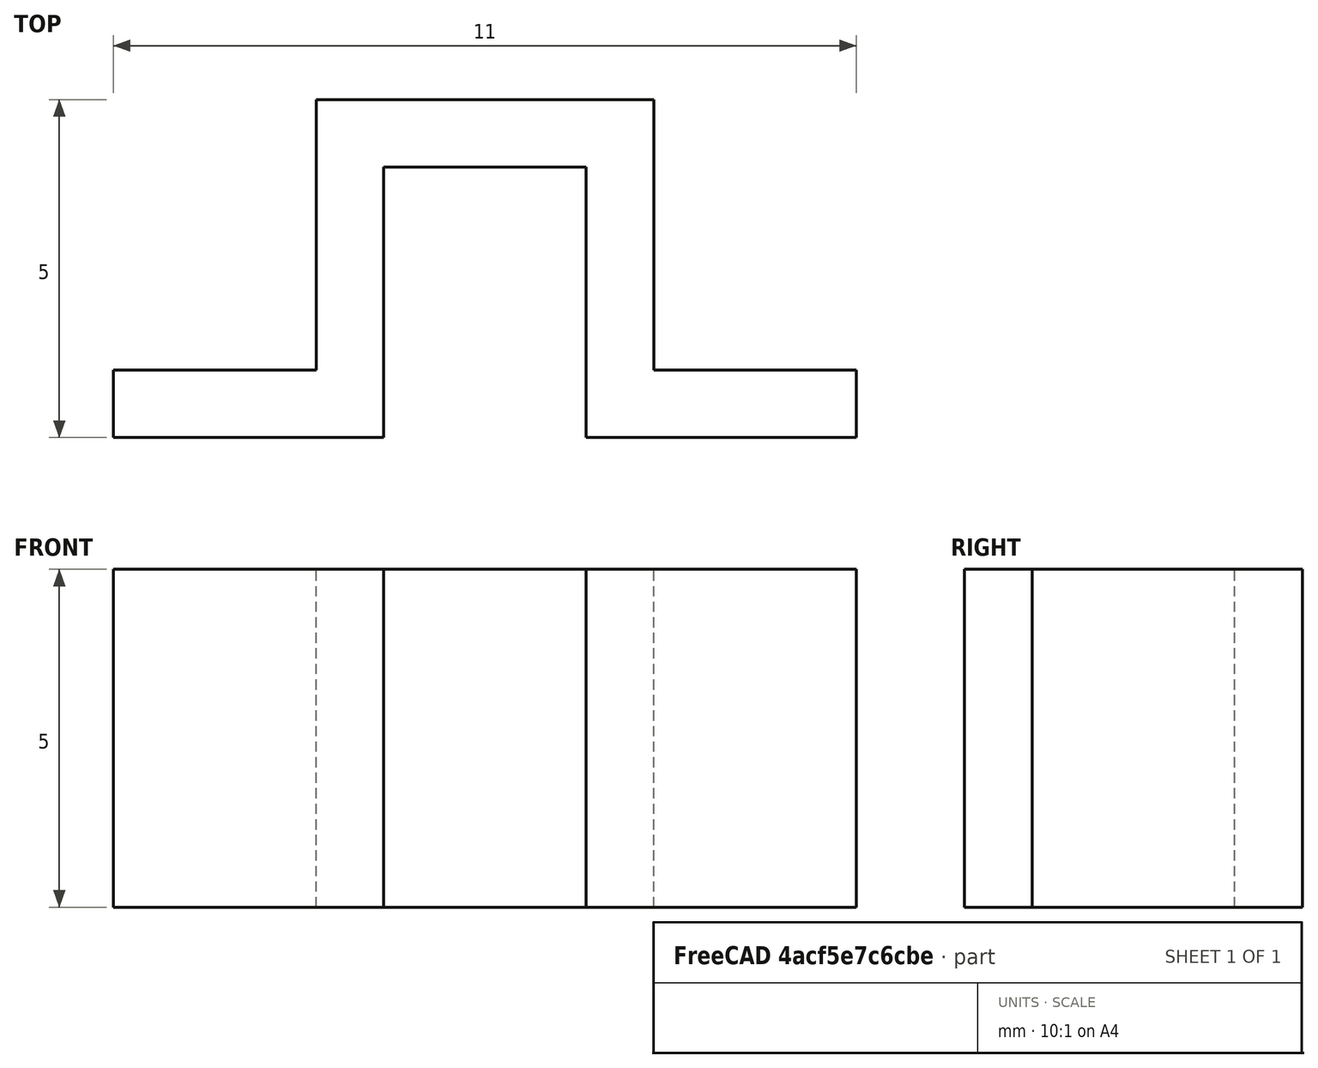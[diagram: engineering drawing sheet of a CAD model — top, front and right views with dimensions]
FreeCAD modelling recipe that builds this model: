
FCSTD DOCUMENT  (FreeCAD 0.19R)
Label: cable-clip
License: All rights reserved
LicenseURL: http://en.wikipedia.org/wiki/All_rights_reserved
objects: Sketcher::SketchObject×1, PartDesign::Pad×1, PartDesign::Body×1
note: 4 computed .brp shape members not serialized (recipe doc carries the construction recipe); baked Part::Feature solids carry a one-line shape summary decoded from their .brp

FEATURE [Sketcher::SketchObject] Sketch
  FullyConstrained = true
  MapMode = 5
  Support = -> [XY_Plane]
  sketch-geometry (13):
    g0: LineSegment StartX=0 StartY=0 StartZ=0 EndX=0 EndY=1 EndZ=0
    g1: LineSegment StartX=0 StartY=1 StartZ=0 EndX=3 EndY=1 EndZ=0
    g2: LineSegment StartX=3 StartY=1 StartZ=0 EndX=3 EndY=5 EndZ=0
    g3: LineSegment StartX=3 StartY=5 StartZ=0 EndX=8 EndY=5 EndZ=0
    g4: LineSegment StartX=8 StartY=5 StartZ=0 EndX=8 EndY=1 EndZ=0
    g5: LineSegment StartX=8 StartY=1 StartZ=0 EndX=11 EndY=1 EndZ=0
    g6: LineSegment StartX=11 StartY=1 StartZ=0 EndX=11 EndY=0 EndZ=0
    g7: LineSegment StartX=11 StartY=0 StartZ=0 EndX=7 EndY=0 EndZ=0
    g8: LineSegment StartX=7 StartY=0 StartZ=0 EndX=7 EndY=4 EndZ=0
    g9: LineSegment StartX=7 StartY=4 StartZ=0 EndX=4 EndY=4 EndZ=0
    g10: LineSegment StartX=4 StartY=4 StartZ=0 EndX=4 EndY=0 EndZ=0
    g11: LineSegment StartX=4 StartY=0 StartZ=0 EndX=0 EndY=0 EndZ=0
    g12: LineSegment StartX=5.5 StartY=5 StartZ=0 EndX=5.5 EndY=0 EndZ=0
  constraints (37):
    c: Coincident(g0,g-1)
    c: PointOnObject(g0,g-2)
    c: Coincident(g1,g0)
    c: Horizontal(g1)
    c: Coincident(g2,g1)
    c: Coincident(g3,g2)
    c: Horizontal(g3)
    c: Coincident(g4,g3)
    c: Vertical(g4)
    c: Coincident(g5,g4)
    c: Horizontal(g5)
    c: Coincident(g6,g5)
    c: PointOnObject(g6,g-1)
    c: Vertical(g6)
    c: Coincident(g7,g6)
    c: PointOnObject(g7,g-1)
    c: Coincident(g8,g7)
    c: Vertical(g8)
    c: Coincident(g9,g8)
    c: Coincident(g10,g9)
    c: PointOnObject(g10,g-1)
    c: Vertical(g10)
    c: Coincident(g11,g10)
    c: Coincident(g11,g0)
    c: Vertical(g2)
    c: DistanceX(g3,g3) = 5
    c: DistanceY(g9,g2) = 1
    c: DistanceX(g2,g9) = 1
    c: PointOnObject(g12,g3)
    c: PointOnObject(g12,g-1)
    c: Symmetric(g2,g3,g12)
    c: Symmetric(g9,g8,g12)
    c: DistanceY(g2,g2) = 4
    c: Equal(g0,g6)
    c: DistanceY(g0,g0) = 1
    c: Equal(g1,g5)
    c: DistanceX(g1,g1) = 3
FEATURE [PartDesign::Pad] Pad
  Direction = (1,1,1)
  Length = 5
  Length2 = 100
  Profile = -> Sketch
  Type = 0
FEATURE [PartDesign::Body] Body
  Group = -> [Sketch,Pad]
  Origin = -> Origin
  Tip = -> Pad
